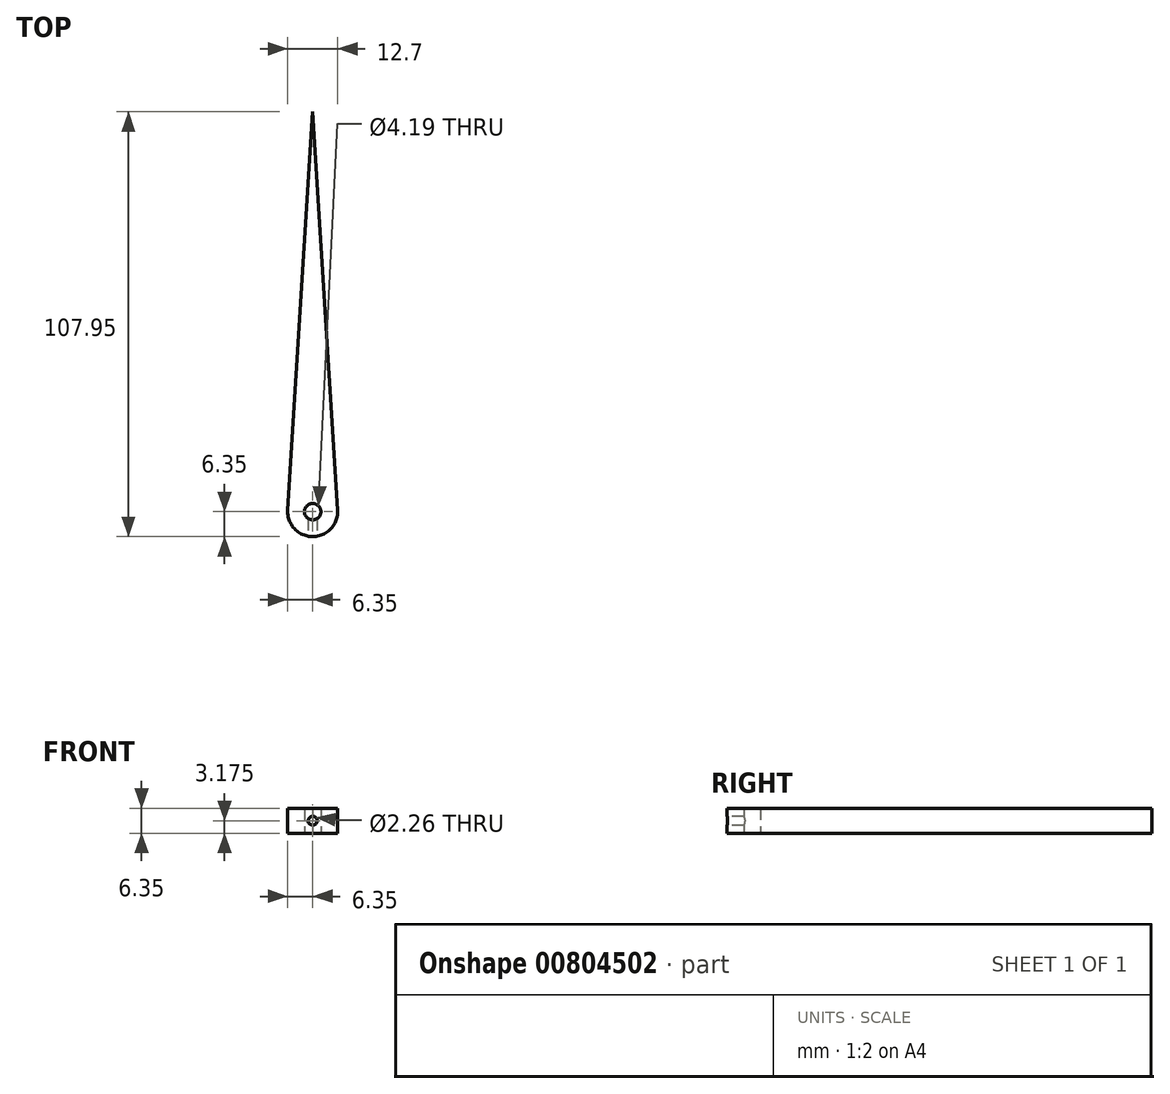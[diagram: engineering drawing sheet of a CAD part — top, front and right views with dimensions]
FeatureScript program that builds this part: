
annotation { "Feature Type Name" : "Feature", "Feature Type Description" : "" }
export const myFeature = defineFeature(function(context is Context, id is Id, definition is map)
    precondition{}
    {
        {
            var Q0;
            Q0=qCreatedBy(makeId("Top.planeOp"),FACE);
            var sketch = newSketch(context, id + "F0", { "sketchPlane" : qUnion([Q0])});
            skCircle(sketch, "E0", {"center": v(0, 0) * mm, "radius": 6.35 * mm});
            skLineSegment(sketch, "E1", {"start": v(-6.34, 0.4) * mm, "end": v(0, 101.6) * mm});
            skLineSegment(sketch, "E2", {"start": v(0, 101.6) * mm, "end": v(6.34, 0.4) * mm});
            skCircle(sketch, "E3", {"center": v(0, 0) * mm, "radius": 2.1 * mm});
            skSolve(sketch);
        }
        {
            var Q0;
            Q0 = qSketchRegion(id + "F0", true);
            extrude(context, id + "F1", {"entities" : qUnion([Q0]), "depth" : 6.35 * mm, "offsetDistance" : 25.4 * mm});
        }
        {
            var Q0;
            Q0=makeQuery(id+"F1.opExtrude","CAP_EDGE",EDGE,{"disambiguationData":[OSD([sQuery(id+"F0.wireOp",EDGE,"E0")])],"isStart":true});
            cPoint(context, id + "F2", {"entities" : qUnion([Q0]), "parameter" : 0.5});
        }
        {
            var Q0;
            Q0=qCreatedBy(makeId("Front.planeOp"),FACE);
            var Q1;
            Q1 = qCreatedBy(id + "F2" ,VERTEX);
            cPlane(context, id + "F3", {"entities" : qUnion([Q0, Q1]), "cplaneType" : CPlaneType.PLANE_POINT, "offset" : 25.4 * mm, "width" : 152.4 * mm, "height" : 152.4 * mm});
        }
        {
            var Q0;
            Q0=qCreatedBy(id+"F3.planeOp",FACE);
            var sketch = newSketch(context, id + "F4", { "sketchPlane" : qUnion([Q0])});
            skLineSegment(sketch, "E4.0", {"start": v(-6.35, 6.35) * mm, "end": v(6.35, 6.35) * mm, "construction": true});
            skLineSegment(sketch, "E5.0", {"start": v(-6.35, 0) * mm, "end": v(6.35, 0) * mm, "construction": true});
            skLineSegment(sketch, "E6", {"start": v(-6.35, 6.35) * mm, "end": v(6.35, 0) * mm, "construction": true});
            skPoint(sketch, "E7", {"position": v(0, 3.18) * mm});
            skSolve(sketch);
        }
        {
            var Q0;
            Q0=sQuery(id+"F4.wireOp",VERTEX,"E7");
            var Q1;
            Q1=makeQuery(id+"F1.opExtrude","SWEPT_BODY",BODY,{"disambiguationData":[OSD([sQuery(id+"F0.wireOp",EDGE,"E0"),sQuery(id+"F0.wireOp",EDGE,"E1"),sQuery(id+"F0.wireOp",EDGE,"E2"),sQuery(id+"F0.wireOp",EDGE,"E3")])]});
            hole(context, id + "F5", {"style" : HoleStyle.SIMPLE, "endStyle" : HoleEndStyle.BLIND, "standardTappedOrClearance" : lookupTablePath({ "standard" : "ANSI", "engagement" : "75%", "pitch" : "40 tpi", "size" : "#4", "type" : "Tapped" }), "standardBlindInLast" : lookupTablePath({ "standard" : "ANSI", "fit" : "Normal", "engagement" : "75%", "pitch" : "40 tpi", "size" : "#4", "type" : "Clearance & tapped" }), "holeDiameter" : 2.26 * mm, "majorDiameter" : 2.84 * mm, "showTappedDepth" : true, "holeDepth" : 5.08 * mm, "isTappedThrough" : true, "tappedDepth" : 5.08 * mm, "tapClearance" : 0, "locations" : qUnion([Q0]), "scope" : qUnion([Q1])});
        }
    });
